# Revit family: AGSRGR
name_source: partatom
category: Electrical Fixtures
units: mm (PartAtom-declared; Revit-internal decimal feet)

## family parameters
Always vertical = Yes
Cut with Voids When Loaded = No
Maintain Annotation Orientation = No
Part Type = Normal
Room Calculation Point = No
Round Connector Dimension = Use Diameter
Shared = No
Work Plane-Based = No

## types (1)
- AGSRGR
    AC Power = 100-120V~ 50/60Hz
    Altitude Rating = 2000m
    Default Elevation = 0.00"
    Description = The AGS RGR Alarm Strobe Relay, is designed to collaborate with the AGS Mini Merlin. 
 
The AGS RGR incorporates three normally closed dry contact signals to multiple boiler safety circuits for alarm 
conditions allowing boilers to shut down. In addition, the RGR has a 24VDC output upon a Mini Merlin alarm condition 
and open/close circuit for external audible alarm silencing buttons. 
 The AGS RGR Alarm Strobe Relay, is designed to collaborate with the AGS Mini Merlin. 
 
The AGS RGR incorporates three normally closed dry contact signals to multiple boiler safety circuits for alarm 
conditions allowing boilers to shut down. In addition, the RGR has a 24VDC output upon a Mini Merlin alarm condition 
and open/close circuit for external audible alarm silencing buttons. 
 The AGS RGR Alarm Strobe Relay, is designed to collaborate with the AGS Mini Merlin. 
 
The AGS RGR incorporates three normally closed dry contact signals to multiple boiler safety circuits for alarm 
conditions allowing boilers to shut down. In addition, the RGR has a 24VDC output upon a Mini Merlin alarm condition 
and open/close circuit for external audible alarm silencing buttons.
    Housing Materials = ABS PA765 (Flame Rating UL94 V-1)
    Internal Fuse = Anti-Surge 3.15A 250Vac
    Manufacturer = American Gas Safety LLC
    Model = AGSRGR
    Operating Temperature = -10 ~ 50°C / 14 ~ 122°F   30 ~ 80% RH (non-condensing)
    Power Consumptions = 3W max without Strobe.
    Size: (H x W x D) = 5.95 x 4.37 x 1.97” (151 x 111 x 50mm)
    Storage = -25 ~ 50°C / -13~122F° up to 95% RH (non-condensing)
    Tel = (727) 608-4375
    Typical = Min. 18AWG / 75°C min / Tinned copper.
    Weight = 0.72lbs (325g)

## geometry (parser evidence)
native form markers: Sweep x40
no freeform markers — native parametric forms only
